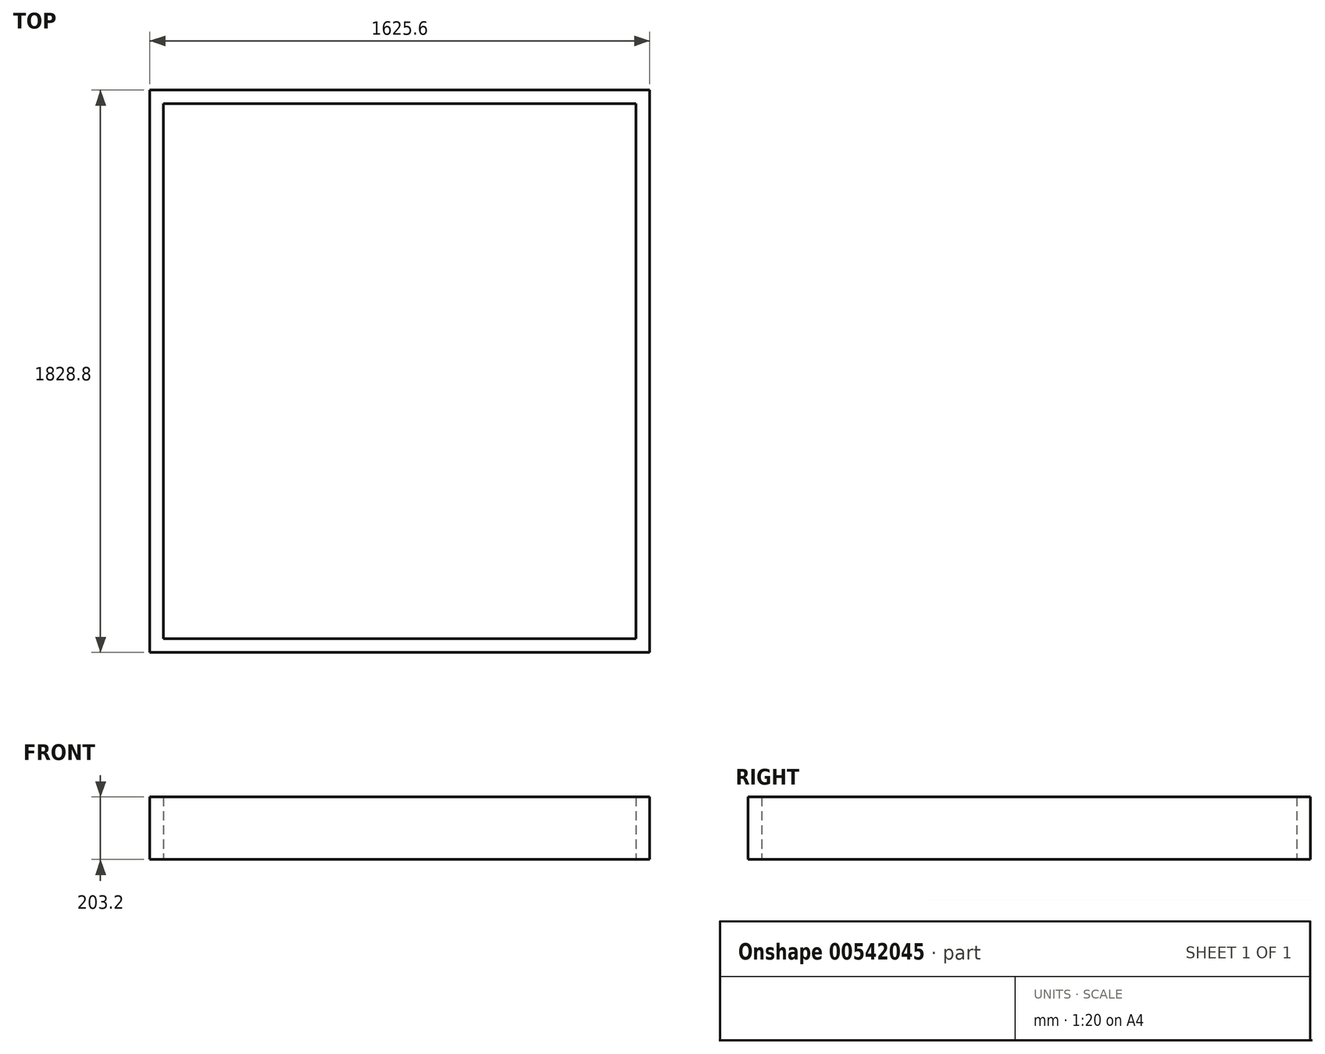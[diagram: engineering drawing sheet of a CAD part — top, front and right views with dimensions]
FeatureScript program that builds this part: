
annotation { "Feature Type Name" : "Feature", "Feature Type Description" : "" }
export const myFeature = defineFeature(function(context is Context, id is Id, definition is map)
    precondition{}
    {
        {
            var Q0;
            Q0=qCreatedBy(makeId("Top.planeOp"),FACE);
            var sketch = newSketch(context, id + "F0", { "sketchPlane" : qUnion([Q0])});
            skLineSegment(sketch, "E0.bottom", {"start": v(-812.8, 914.4) * mm, "end": v(812.8, 914.4) * mm});
            skLineSegment(sketch, "E0.top", {"start": v(-812.8, -914.4) * mm, "end": v(812.8, -914.4) * mm});
            skLineSegment(sketch, "E0.left", {"start": v(-812.8, 914.4) * mm, "end": v(-812.8, -914.4) * mm});
            skLineSegment(sketch, "E0.right", {"start": v(812.8, 914.4) * mm, "end": v(812.8, -914.4) * mm});
            skPoint(sketch, "E0.middle", {"position": v(0, 0) * mm});
            skLineSegment(sketch, "E1.bottom", {"start": v(-768.35, 869.95) * mm, "end": v(768.35, 869.95) * mm});
            skLineSegment(sketch, "E1.top", {"start": v(-768.35, -869.95) * mm, "end": v(768.35, -869.95) * mm});
            skLineSegment(sketch, "E1.left", {"start": v(-768.35, 869.95) * mm, "end": v(-768.35, -869.95) * mm});
            skLineSegment(sketch, "E1.right", {"start": v(768.35, 869.95) * mm, "end": v(768.35, -869.95) * mm});
            skSolve(sketch);
        }
        {
            var Q0;
            Q0=qSketchRegion(id+"F0",true);
            extrude(context, id + "F1", {"entities" : qUnion([Q0]), "depth" : 203.2 * mm, "offsetDistance" : 25.4 * mm});
        }
    });
